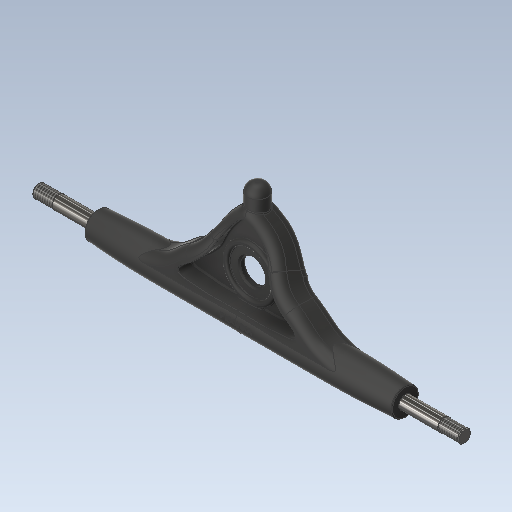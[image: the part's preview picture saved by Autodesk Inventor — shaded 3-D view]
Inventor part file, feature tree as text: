
AUTODESK INVENTOR PART (.ipt)
format: ipt  version: 2020.1 (Build 241239000, 239)  size: 7,095,296 bytes
history: native  units: mm
features: sketch x12, extrude x12, fillet x10, other x4, chamfer x3, plane x3, thread x2, revolve x1, thicken_offset x1, surface_op x1
ambient origin geometry x8: Origin, YZ Plane, XZ Plane, XY Plane, X Axis, Y Axis, Z Axis, Center Point
bodies: Solid1 (feature_tree)
feature tree (49):
  revolve  "Revolution1"  [1 undecoded]
  sketch  "Sketch2"  dims[d20=9.5mm d21=8.0mm d29=9.4mm]
  sketch  "Sketch3"  dims[d32=8.4mm d33=9.0mm d34=9.5mm d35=9.5mm]
  thicken_offset  "Thicken2"
  extrude  "Extrusion2"  Depth=8.0mm
  fillet  "Fillet1"  Radius=9.4mm
  extrude  "Extrusion3"  Depth=9.0mm
  fillet  "Fillet2"  Radius=9.5mm
  fillet  "Fillet3"  Radius=9.5mm
  extrude  "Extrusion4"  Depth=15.0mm
  fillet  "Fillet4"  Radius=25.0mm
  extrude  "Extrusion5"  Depth=15.0mm
  fillet  "Fillet5"  Radius=65.0mm
  extrude  "Extrusion6"  TaperAngle=90.0deg  [1 undecoded]
  fillet  "Fillet6"  [1 undecoded]
  fillet  "Fillet7"  Radius=18.0mm
  chamfer  "Chamfer1"  Distance=10.0mm
  extrude  "Extrusion8"  Depth=59.0mm
  fillet  "Fillet10"  Radius=10.0mm
  fillet  "Fillet11"  Radius=0.5mm
  extrude  "Extrusion9"  Depth=4.0mm TaperAngle=0.0deg
  extrude  "Extrusion10"  Depth=6.0mm TaperAngle=0.0deg
  chamfer  "Chamfer2"  Distance=6.0mm
  extrude  "Extrusion11"  Depth=0.5mm
  extrude  "Extrusion12"  Depth=0.5mm
  chamfer  "Chamfer3"  Distance=1.0mm Angle=45.0deg
  plane  "Work Plane2"
  sketch  "Sketch12"  dims[d145=1.0mm d146=6.0mm d147=2.0mm d148=0.0mm d149=0.0mm]
  plane  "Work Plane3"
  sketch  "Sketch13"  dims[d150=1.5mm d151=6.0mm d152=0.0mm d153=0.5mm d154=0.5mm d155=1.0mm d156=2.0mm d157=45.0deg d158=7.5mm d159=12.0mm d166=10.0mm d167=5.0mm d168=0.0mm d169=0.0mm d170=1.0mm d171=5.0mm d172=8.0mm d173=35.0mm d174=0.0mm d175=0.1mm d176=12.0mm d177=0.0mm d178=0.5mm d179=2.0mm d180=45.0deg d181=8.0mm d182=35.0mm d183=0.0mm d184=0.1mm d185=12.0mm d186=0.0mm d187=0.5mm d188=2.0mm d189=45.0deg d192=7.0mm d193=7.0mm d194=0.5mm d195=0.0mm d196=0.5mm d197=0.0mm d198=10.0mm d199=0.0mm d200=10.0mm d201=0.0mm d203=30.5mm d204=0.5mm d205=22.455406mm]
  extrude  "Extrusion13"  Depth=7.5mm
  extrude  "Extrusion14"  Depth=12.0mm
  thread  "Thread1"  [1 undecoded]
  thread  "Thread2"  [1 undecoded]
  fillet  "Fillet13"  Radius=5.0mm
  plane  "Work Plane5"
  sketch  "Sketch1"  dims[d1=65.0mm d2=90.5mm]
  other  "Image1"
  other  "Image4"
  sketch  "Sketch4"  dims[d37=90.0deg d38=15.0mm d39=25.0mm]
  sketch  "3D Sketch2"
  other  "3D Intersection2"
  other  "Srf2"
  sketch  "Sketch6"  dims[d40=32.0mm d41=15.0mm d123=65.0mm]
  sketch  "Sketch7"  dims[d124=15.0mm d125=90.0deg d132=0.0mm d133=18.0mm]
  sketch  "Sketch9"  dims[d134=18.0mm d135=10.0mm d136=0.0mm]
  sketch  "Sketch10"  dims[d137=5.0mm d138=59.0mm d139=10.0mm d140=0.0mm d141=0.5mm]
  sketch  "Sketch11"  dims[d142=0.5mm d143=4.0mm d144=0.0mm]
  surface_op  "Boundary Patch2"
note: 5 required parameter values undecoded (feature->parameter linkage not recoverable at this tier; creation-order binding heuristic only, values carry confidence <= 0.55)